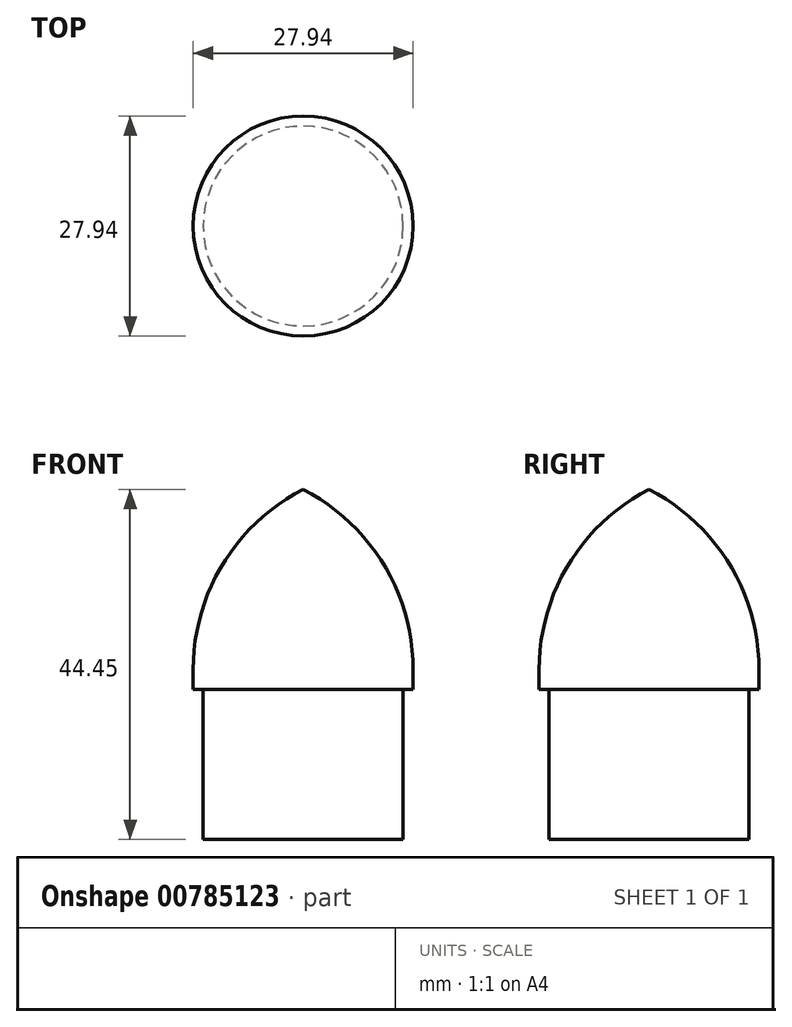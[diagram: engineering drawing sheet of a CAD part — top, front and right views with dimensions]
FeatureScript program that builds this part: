
annotation { "Feature Type Name" : "Feature", "Feature Type Description" : "" }
export const myFeature = defineFeature(function(context is Context, id is Id, definition is map)
    precondition{}
    {
        {
            var Q0;
            Q0=qCreatedBy(makeId("Front.planeOp"),FACE);
            var sketch = newSketch(context, id + "F0", { "sketchPlane" : qUnion([Q0])});
            skLineSegment(sketch, "E0", {"start": v(0, 44.45) * mm, "end": v(0, 0) * mm});
            skArc(sketch, "E1", {"start": v(13.97, 21.59) * mm, "mid": v(10.2, 34.99) * mm, "end": v(0, 44.45) * mm});
            skLineSegment(sketch, "E2", {"start": v(0, 0) * mm, "end": v(12.7, 0) * mm});
            skLineSegment(sketch, "E3", {"start": v(12.7, 0) * mm, "end": v(12.7, 19.05) * mm});
            skLineSegment(sketch, "E4", {"start": v(12.7, 19.05) * mm, "end": v(13.97, 19.05) * mm});
            skLineSegment(sketch, "E5", {"start": v(13.97, 19.05) * mm, "end": v(13.97, 21.59) * mm});
            skLineSegment(sketch, "E6", {"start": v(0, 0) * mm, "end": v(0, -13.18) * mm, "construction": true});
            skSolve(sketch);
        }
        {
            var Q0;
            Q0 = qSketchRegion(id + "F0", true);
            var Q1;
            Q1=sQuery(id+"F0.wireOp",EDGE,"E6");
            revolve(context, id + "F1", {"surfaceOperationType" : NewSurfaceOperationType.NEW, "entities" : qUnion([Q0]), "axis" : qUnion([Q1]), "revolveType" : RevolveType.FULL});
        }
    });
